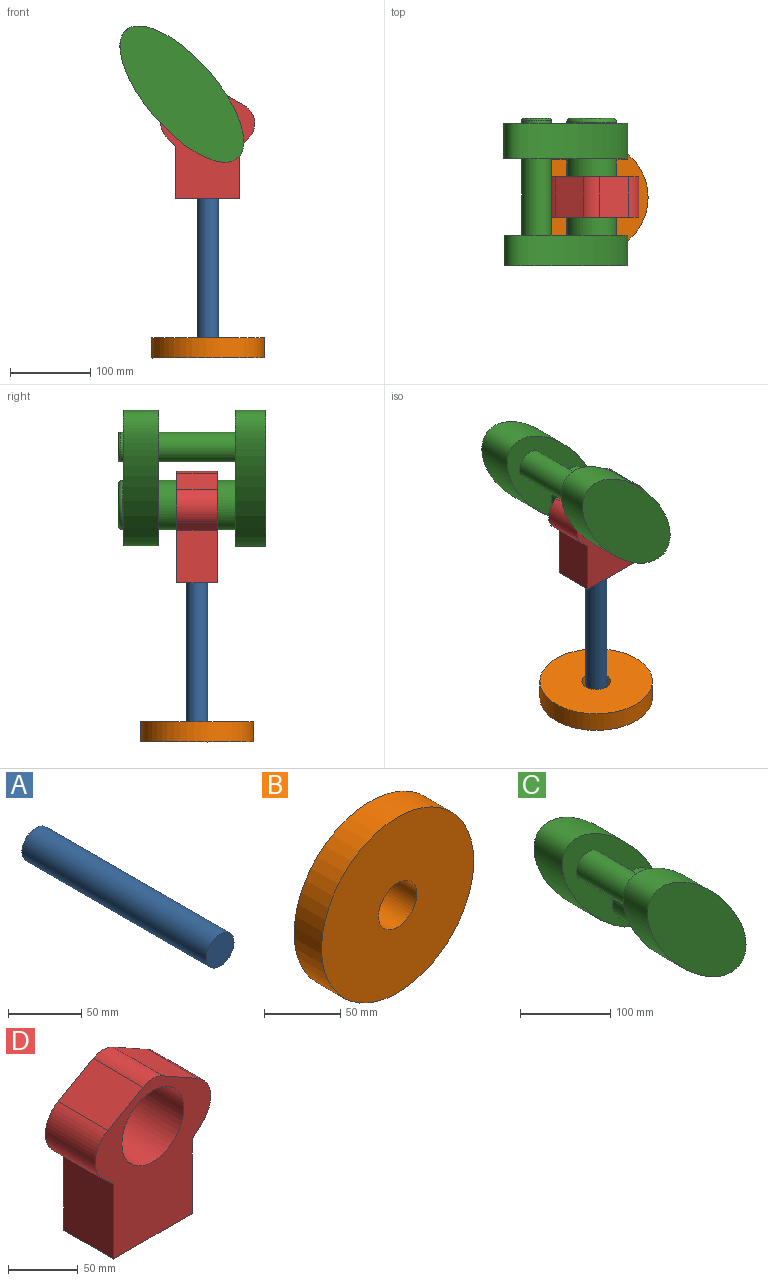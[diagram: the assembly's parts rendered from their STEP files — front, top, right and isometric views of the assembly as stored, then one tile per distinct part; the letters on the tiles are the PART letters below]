
ASSEMBLY  parts=4 mates=3
PART A: 3 faces, bbox 26.8x177.8x26.8 mm
  f0: cylinder r=13.42mm len=177.8mm, axis (0,1,0), area 14987.8mm2, adj f1,f2
  f1: plane 26.83x26.83mm, normal (0,-1,0), area 565.5mm2, adj f0
  f2: plane 26.83x26.83mm, normal (0,1,0), area 565.5mm2, adj f0
PART B: 4 faces, bbox 140.7x25.4x140.7 mm
  f0: cylinder r=70.33mm len=140.65mm, axis (0,1,0), area 11223.7mm2, adj f1,f2
  f1: plane 140.65x140.65mm, normal (0,-1,0), area 14545.4mm2, adj f0,f3
  f2: plane 140.65x140.65mm, normal (0,1,0), area 14545.4mm2, adj f0,f3
  f3: cylinder r=17.77mm len=35.55mm, axis (0,1,0), area 2836.6mm2, adj f1,f2
PART C: 14 faces, bbox 154.9x184.2x170.4 mm
  f0: cylinder r=30.99mm len=95.25mm, axis (0,1,0), area 18546.4mm2, adj f3,f10
  f1: cylinder r=18.52mm len=95.25mm, axis (0,1,0), area 11086.7mm2, adj f3,f10
  f2: extruded ~169.2x154.77mm, area 21847.5mm2, adj f3,f4
  f3: plane 169.36x154.94mm, normal (0,-1,0), area 10511.4mm2, adj f0,f1,f2
  f4: plane 169.36x154.94mm, normal (0,1,0), area 10511.4mm2, adj f2,f6,f8
  f5: plane 51.82x51.82mm, normal (0,1,0), area 2109mm2, adj f13
  f6: cylinder r=30.99mm len=61.98mm, axis (0,1,0), area 247.3mm2, adj f4,f13
  f7: plane 31.97x31.97mm, normal (0,1,0), area 802.7mm2, adj f12
  f8: cylinder r=18.52mm len=37.05mm, axis (0,1,0), area 443.5mm2, adj f4,f12
  f9: extruded ~170.2x154.25mm, area 18775.9mm2, adj f10,f11
  f10: plane 170.36x154.49mm, normal (0,1,0), area 10689.2mm2, adj f0,f1,f9
  f11: plane 170.36x154.49mm, normal (0,-1,0), area 14784.3mm2, adj f9
  f12: torus R=15.98mm, axis (0,1,0), area 441.3mm2, adj f7,f8
  f13: torus R=25.91mm, axis (0,1,0), area 1461.2mm2, adj f5,f6
PART D: 13 faces, bbox 117.4x50.8x139 mm
  f0: plane 65.72x50.8mm, normal (-1,0,0), area 3338.5mm2, adj f1,f6,f7,f8
  f1: plane 80.25x50.8mm, normal (0,0,-1), area 4076.7mm2, adj f0,f2,f7,f8
  f2: plane 65.72x50.8mm, normal (1,0,0), area 3338.5mm2, adj f1,f3,f7,f8
  f3: plane 50.8x10.47mm, normal (0.68,0,-0.73), area 725.8mm2, adj f2,f7,f8,f10
  f4: plane 50.8x35.92mm, normal (0.49,0,0.87), area 2094.6mm2, adj f7,f8,f9,f10
  f5: plane 50.8x35.67mm, normal (-0.49,0,0.87), area 2082.8mm2, adj f7,f8,f9,f11
  f6: plane 50.8x10.49mm, normal (-0.68,0,-0.73), area 728.9mm2, adj f0,f7,f8,f11
  f7: plane 139.04x117.39mm, normal (0,1,0), area 8745.1mm2, adj f0,f1,f2,f3,f4,f5,f6,f9
  f8: plane 139.04x117.39mm, normal (0,-1,0), area 8745.1mm2, adj f0,f1,f2,f3,f4,f5,f6,f9
  f9: cylinder r=20.32mm len=50.8mm, axis (0,-1,0), area 1062mm2, adj f4,f5,f7,f8
  f10: cylinder r=25.4mm len=50.8mm, axis (0,-1,0), area 2425.5mm2, adj f3,f4,f7,f8
  f11: cylinder r=25.4mm len=50.8mm, axis (0,-1,0), area 2419.5mm2, adj f5,f6,f7,f8
  f12: cylinder r=31.4mm len=62.81mm, axis (0,1,0), area 10023.3mm2, adj f7,f8
PLACE A rot(axis=(1,0,0),90deg) t=(96.72,214.64,-208.66)mm
PLACE B rot(axis=(-1,0,0),90deg) t=(96.72,214.64,-407.71)mm
PLACE C t=(64.35,268.62,-78.06)mm
PLACE D t=(96.56,189.24,-142.94)mm
MATE fastened A.f0 <-> D.f1  axis (0,0,1) through (96.72,214.64,-208.66)mm
MATE revolute C.f0 <-> D.f12  axis (0,1,0) through (96.56,214.64,-111.61)mm
MATE slider B.f0 <-> A.f0  axis (0,0,1) through (96.72,214.64,-382.31)mm
